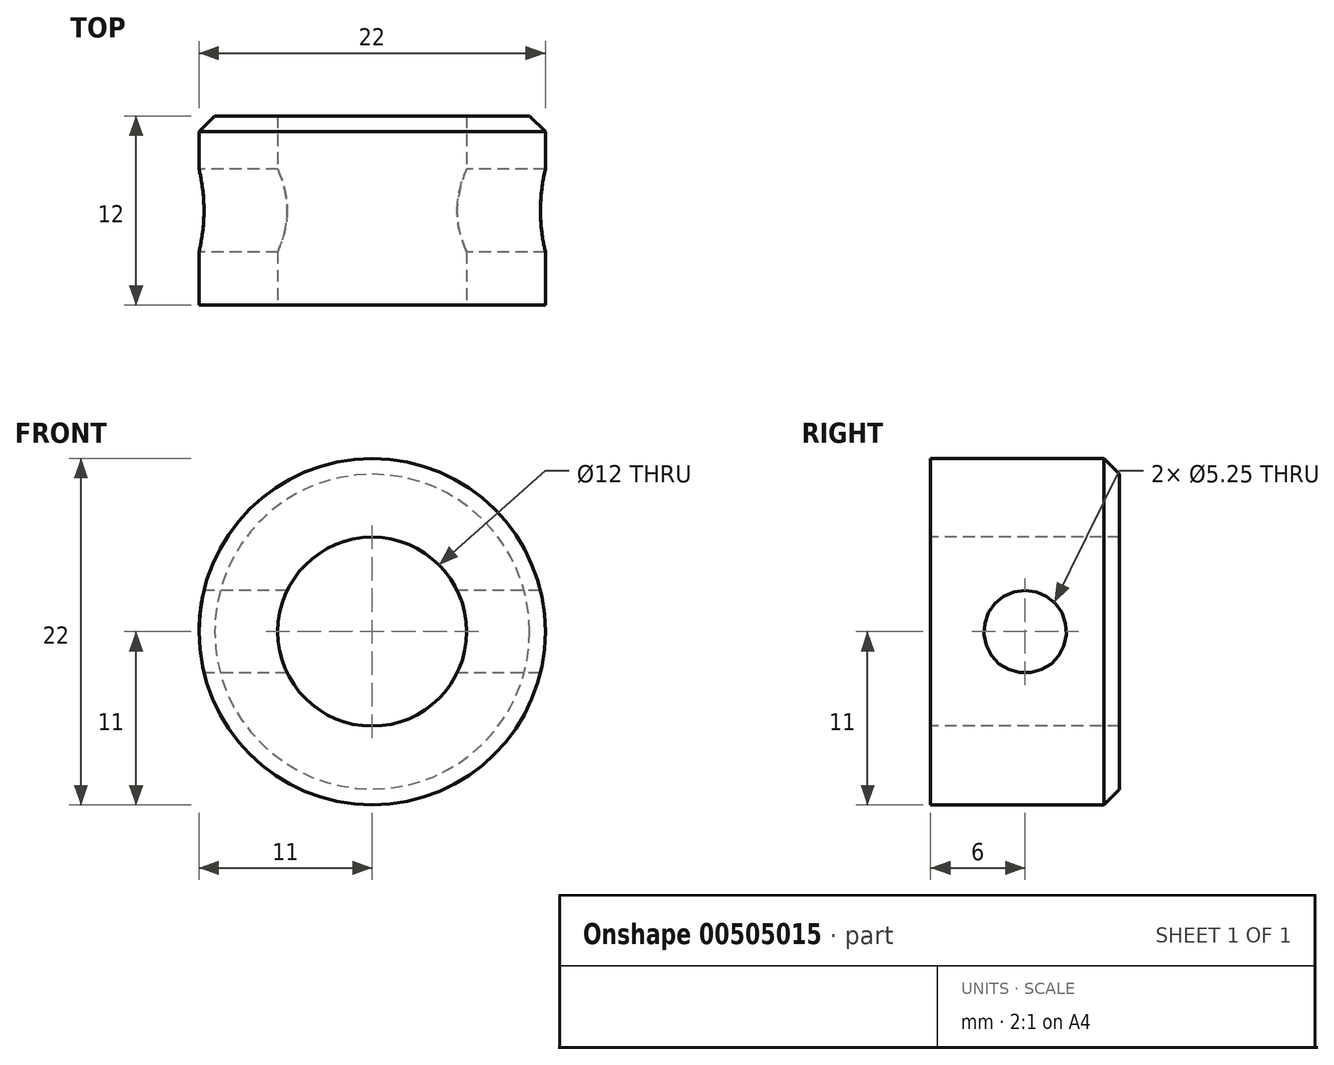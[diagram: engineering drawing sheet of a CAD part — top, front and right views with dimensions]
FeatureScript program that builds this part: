
annotation { "Feature Type Name" : "Feature", "Feature Type Description" : "" }
export const myFeature = defineFeature(function(context is Context, id is Id, definition is map)
    precondition{}
    {
        {
            var Q0;
            Q0=qCreatedBy(makeId("Front.planeOp"),FACE);
            var sketch = newSketch(context, id + "F0", { "sketchPlane" : qUnion([Q0])});
            skCircle(sketch, "E0", {"center": v(0, 0) * mm, "radius": 6 * mm});
            skCircle(sketch, "E1", {"center": v(0, 0) * mm, "radius": 11 * mm});
            skSolve(sketch);
        }
        {
            var Q0;
            Q0=makeQuery(id+"F0.imprint","IMPRINT",FACE,{"disambiguationData":[TD([[makeQuery(id+"F0.imprint","IMPRINT",EDGE,{"derivedFrom":sQuery(id+"F0.wireOp",EDGE,"E0")}),-1.0]])]});
            extrude(context, id + "F1", {"entities" : qUnion([Q0]), "oppositeDirection" : true, "depth" : 12 * mm, "offsetDistance" : 25 * mm});
        }
        {
            var Q0;
            Q0=makeQuery(id+"F1.opExtrude","CAP_EDGE",EDGE,{"disambiguationData":[OSD([sQuery(id+"F0.wireOp",EDGE,"E1")])],"isStart":false});
            chamfer(context, id + "F2", {"entities" : qUnion([Q0]), "width" : 1 * mm, "tangentPropagation" : true});
        }
        {
            var Q0;
            Q0=qCreatedBy(makeId("Right.planeOp"),FACE);
            var sketch = newSketch(context, id + "F3", { "sketchPlane" : qUnion([Q0])});
            skCircle(sketch, "E2", {"center": v(6, 0) * mm, "radius": 3 * mm});
            skCircle(sketch, "E3", {"center": v(6, 0) * mm, "radius": 2.62 * mm});
            skSolve(sketch);
        }
        {
            var Q0;
            Q0=makeQuery(id+"F3.imprint","IMPRINT",FACE,{"disambiguationData":[TD([[makeQuery(id+"F3.imprint","IMPRINT",EDGE,{"derivedFrom":sQuery(id+"F3.wireOp",EDGE,"E3")}),1.0]])]});
            var Q1;
            Q1=sQuery(id+"F3.wireOp",EDGE,"E3");
            extrude(context, id + "F4", {"entities" : qUnion([Q0]), "operationType" : NewBodyOperationType.REMOVE, "surfaceEntities" : qUnion([Q1]), "endBound" : BoundingType.SYMMETRIC, "depth" : 25 * mm, "offsetDistance" : 25 * mm});
        }
    });
